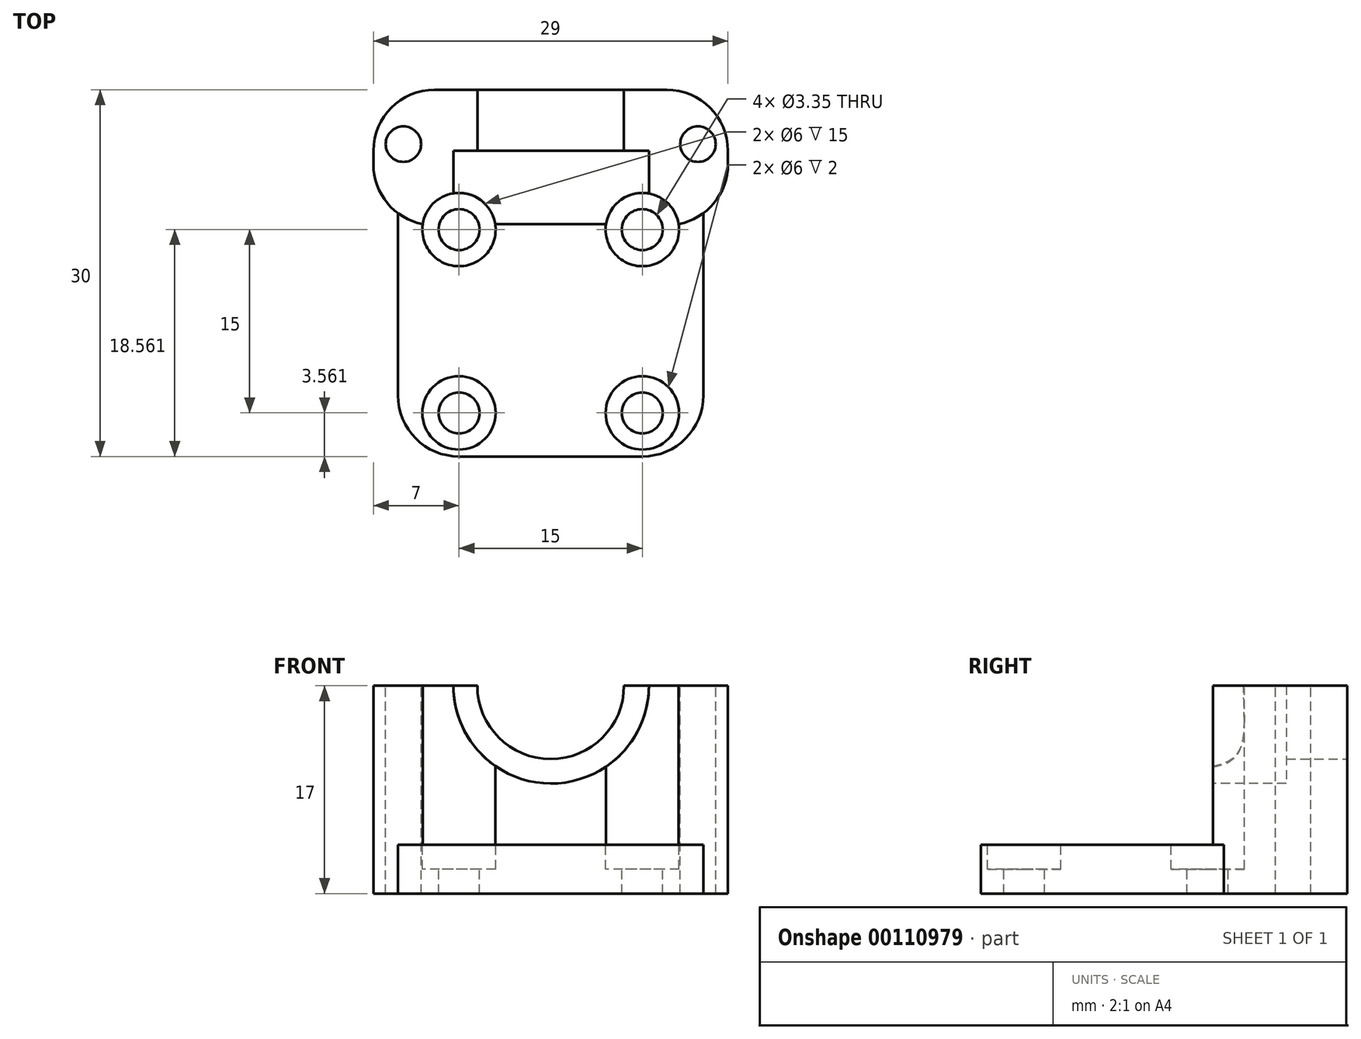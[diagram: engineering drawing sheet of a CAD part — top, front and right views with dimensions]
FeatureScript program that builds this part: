
annotation { "Feature Type Name" : "Feature", "Feature Type Description" : "" }
export const myFeature = defineFeature(function(context is Context, id is Id, definition is map)
    precondition{}
    {
        {
            var Q0;
            Q0=qCreatedBy(makeId("Top.planeOp"),FACE);
            var sketch = newSketch(context, id + "F0", { "sketchPlane" : qUnion([Q0])});
            skLineSegment(sketch, "E0.bottom", {"start": v(0, 0) * mm, "end": v(25, 0) * mm});
            skLineSegment(sketch, "E0.top", {"start": v(0, 30) * mm, "end": v(25, 30) * mm});
            skLineSegment(sketch, "E0.left", {"start": v(0, 0) * mm, "end": v(0, 30) * mm});
            skLineSegment(sketch, "E0.right", {"start": v(25, 0) * mm, "end": v(25, 30) * mm});
            skSolve(sketch);
        }
        {
            var Q0;
            Q0=qSketchRegion(id+"F0",true);
            extrude(context, id + "F1", {"entities" : qUnion([Q0]), "depth" : 4 * mm});
        }
        {
            var Q0;
            Q0=makeQuery(id+"F1.opExtrude","CAP_FACE",FACE,{"disambiguationData":[OSD([sQuery(id+"F0.wireOp",EDGE,"E0.bottom"),sQuery(id+"F0.wireOp",EDGE,"E0.top"),sQuery(id+"F0.wireOp",EDGE,"E0.left"),sQuery(id+"F0.wireOp",EDGE,"E0.right")])],"isStart":false});
            var sketch = newSketch(context, id + "F2", { "sketchPlane" : qUnion([Q0])});
            skLineSegment(sketch, "E1.bottom", {"start": v(0, 30) * mm, "end": v(25, 30) * mm});
            skLineSegment(sketch, "E1.top", {"start": v(0, 19) * mm, "end": v(25, 19) * mm});
            skLineSegment(sketch, "E1.left", {"start": v(0, 30) * mm, "end": v(0, 19) * mm});
            skLineSegment(sketch, "E1.right", {"start": v(25, 30) * mm, "end": v(25, 19) * mm});
            skSolve(sketch);
        }
        {
            var Q0;
            Q0=qSketchRegion(id+"F2",true);
            extrude(context, id + "F3", {"entities" : qUnion([Q0]), "operationType" : NewBodyOperationType.ADD, "depth" : 13 * mm});
        }
        {
            var Q0;
            Q0=makeQuery(id+"F1.opExtrude","CAP_FACE",FACE,{"disambiguationData":[OSD([sQuery(id+"F0.wireOp",EDGE,"E0.bottom"),sQuery(id+"F0.wireOp",EDGE,"E0.top"),sQuery(id+"F0.wireOp",EDGE,"E0.left"),sQuery(id+"F0.wireOp",EDGE,"E0.right")])],"isStart":false});
            var sketch = newSketch(context, id + "F4", { "sketchPlane" : qUnion([Q0])});
            skCircle(sketch, "E2", {"center": v(5, 18.56) * mm, "radius": 1.68 * mm});
            skCircle(sketch, "E3", {"center": v(20, 18.56) * mm, "radius": 1.68 * mm});
            skCircle(sketch, "E4", {"center": v(5, 3.56) * mm, "radius": 1.68 * mm});
            skCircle(sketch, "E5", {"center": v(20, 3.56) * mm, "radius": 1.68 * mm});
            skLineSegment(sketch, "E6", {"start": v(5, 18.56) * mm, "end": v(0, 18.56) * mm});
            skLineSegment(sketch, "E7", {"start": v(20, 3.56) * mm, "end": v(25, 3.56) * mm});
            skCircle(sketch, "E8", {"center": v(5, 18.56) * mm, "radius": 3 * mm});
            skCircle(sketch, "E9", {"center": v(20, 18.56) * mm, "radius": 3 * mm});
            skCircle(sketch, "E10", {"center": v(5, 3.56) * mm, "radius": 3 * mm});
            skCircle(sketch, "E11", {"center": v(20, 3.56) * mm, "radius": 3 * mm});
            skSolve(sketch);
        }
        {
            var Q0;
            Q0=makeQuery(id+"F4.imprint","IMPRINT",FACE,{"disambiguationData":[TD([[makeQuery(id+"F4.imprint","IMPRINT",EDGE,{"derivedFrom":sQuery(id+"F4.wireOp",EDGE,"E2")}),1.0]])]});
            var Q1;
            Q1=makeQuery(id+"F4.imprint","IMPRINT",FACE,{"disambiguationData":[TD([[makeQuery(id+"F4.imprint","IMPRINT",EDGE,{"derivedFrom":sQuery(id+"F4.wireOp",EDGE,"E3")}),1.0]])]});
            var Q2;
            Q2=makeQuery(id+"F4.imprint","IMPRINT",FACE,{"disambiguationData":[TD([[makeQuery(id+"F4.imprint","IMPRINT",EDGE,{"derivedFrom":sQuery(id+"F4.wireOp",EDGE,"E5")}),1.0]])]});
            var Q3;
            Q3=makeQuery(id+"F4.imprint","IMPRINT",FACE,{"disambiguationData":[TD([[makeQuery(id+"F4.imprint","IMPRINT",EDGE,{"derivedFrom":sQuery(id+"F4.wireOp",EDGE,"E4")}),1.0]])]});
            var Q4;
            {var subQ0=sQuery(id+"F4.wireOp",EDGE,"E2");var subQ1=makeQuery(id+"F3.opExtrude","CAP_EDGE",EDGE,{"disambiguationData":[OSD([sQuery(id+"F2.wireOp",EDGE,"E1.top")])],"isStart":true});var subQ2=makeQuery(id+"F4.imprint","INTERSECT",VERTEX,{"disambiguationData":[OD(0.0)],"derivedFrom":[subQ1,subQ0]});Q4=makeQuery(id+"F4.imprint","IMPRINT",FACE,{"disambiguationData":[TD([[makeQuery(id+"F4.imprint","IMPRINT",EDGE,{"disambiguationData":[TD([[subQ2,1.0]])],"derivedFrom":subQ0}),1.0]])]});}
            extrude(context, id + "F5", {"entities" : qUnion([Q0, Q1, Q2, Q3, Q4]), "operationType" : NewBodyOperationType.REMOVE, "oppositeDirection" : true, "depth" : 25 * mm, "hasSecondDirection" : true, "secondDirectionOppositeDirection" : false, "secondDirectionDepth" : 25 * mm});
        }
        {
            var Q0;
            Q0=makeQuery(id+"F3.boolean.opBoolean","MERGE",FACE,{"derivedFrom":[makeQuery(id+"F1.opExtrude","SWEPT_FACE",FACE,{"disambiguationData":[OSD([sQuery(id+"F0.wireOp",EDGE,"E0.top")])]}),makeQuery(id+"F3.opExtrude","SWEPT_FACE",FACE,{"disambiguationData":[OSD([sQuery(id+"F2.wireOp",EDGE,"E1.bottom")])]})]});
            var sketch = newSketch(context, id + "F6", { "sketchPlane" : qUnion([Q0])});
            skCircle(sketch, "E12", {"center": v(-12.5, 17) * mm, "radius": 6 * mm});
            skSolve(sketch);
        }
        {
            var Q0;
            {var subQ0=makeQuery(id+"F3.opExtrude","CAP_EDGE",EDGE,{"disambiguationData":[OSD([sQuery(id+"F2.wireOp",EDGE,"E1.bottom")])],"isStart":false});var subQ1=sQuery(id+"F6.wireOp",EDGE,"E12");var subQ3=makeQuery(id+"F6.imprint","INTERSECT",VERTEX,{"disambiguationData":[OD(0.0)],"derivedFrom":[subQ0,subQ1]});Q0=makeQuery(id+"F6.imprint","IMPRINT",FACE,{"disambiguationData":[TD([[makeQuery(id+"F6.imprint","IMPRINT",EDGE,{"disambiguationData":[TD([[subQ3,1.0]])],"derivedFrom":subQ1}),1.0]])]});}
            extrude(context, id + "F7", {"entities" : qUnion([Q0]), "operationType" : NewBodyOperationType.REMOVE, "oppositeDirection" : true, "depth" : 6 * mm});
        }
        {
            var Q0;
            Q0=makeQuery(id+"F3.opExtrude","SWEPT_FACE",FACE,{"disambiguationData":[OSD([sQuery(id+"F2.wireOp",EDGE,"E1.top")])]});
            var sketch = newSketch(context, id + "F8", { "sketchPlane" : qUnion([Q0])});
            skCircle(sketch, "E13", {"center": v(12.54, 17) * mm, "radius": 8 * mm});
            skSolve(sketch);
        }
        {
            var Q0;
            Q0=qSketchRegion(id+"F8",true);
            extrude(context, id + "F9", {"entities" : qUnion([Q0]), "operationType" : NewBodyOperationType.REMOVE, "oppositeDirection" : true, "depth" : 6 * mm});
        }
        {
            var Q0;
            Q0=makeQuery(id+"F4.imprint","IMPRINT",FACE,{"disambiguationData":[TD([[makeQuery(id+"F4.imprint","IMPRINT",EDGE,{"derivedFrom":sQuery(id+"F4.wireOp",EDGE,"E2")}),-1.0]])]});
            var Q1;
            Q1=makeQuery(id+"F4.imprint","IMPRINT",FACE,{"disambiguationData":[TD([[makeQuery(id+"F4.imprint","IMPRINT",EDGE,{"derivedFrom":sQuery(id+"F4.wireOp",EDGE,"E3")}),-1.0]])]});
            var Q2;
            Q2=makeQuery(id+"F4.imprint","IMPRINT",FACE,{"disambiguationData":[TD([[makeQuery(id+"F4.imprint","IMPRINT",EDGE,{"derivedFrom":sQuery(id+"F4.wireOp",EDGE,"E5")}),-1.0]])]});
            var Q3;
            Q3=makeQuery(id+"F4.imprint","IMPRINT",FACE,{"disambiguationData":[TD([[makeQuery(id+"F4.imprint","IMPRINT",EDGE,{"derivedFrom":sQuery(id+"F4.wireOp",EDGE,"E4")}),-1.0]])]});
            extrude(context, id + "F10", {"entities" : qUnion([Q0, Q1, Q2, Q3]), "operationType" : NewBodyOperationType.REMOVE, "oppositeDirection" : true, "depth" : 2 * mm, "hasSecondDirection" : true, "secondDirectionOppositeDirection" : false, "secondDirectionDepth" : 25 * mm});
        }
        {
            var Q0;
            Q0=makeQuery(id+"F1.opExtrude","SWEPT_EDGE",EDGE,{"disambiguationData":[OSD([sQuery(id+"F0.wireOp",EDGE,"E0.bottom"),sQuery(id+"F0.wireOp",EDGE,"E0.left")])]});
            var Q1;
            Q1=makeQuery(id+"F1.opExtrude","SWEPT_EDGE",EDGE,{"disambiguationData":[OSD([sQuery(id+"F0.wireOp",EDGE,"E0.bottom"),sQuery(id+"F0.wireOp",EDGE,"E0.right")])]});
            fillet(context, id + "F11", {"entities" : qUnion([Q0, Q1]), "radius" : 5 * mm, "tangentPropagation" : true, "allowEdgeOverflow" : false});
        }
        {
            var Q0;
            Q0=makeQuery(id+"F3.boolean.opBoolean","MERGE",FACE,{"derivedFrom":[makeQuery(id+"F1.opExtrude","SWEPT_FACE",FACE,{"disambiguationData":[OSD([sQuery(id+"F0.wireOp",EDGE,"E0.left")])]}),makeQuery(id+"F3.opExtrude","SWEPT_FACE",FACE,{"disambiguationData":[OSD([sQuery(id+"F2.wireOp",EDGE,"E1.left")])]})]});
            var sketch = newSketch(context, id + "F12", { "sketchPlane" : qUnion([Q0])});
            skLineSegment(sketch, "E14.bottom", {"start": v(-30, 0) * mm, "end": v(-19, 0) * mm});
            skLineSegment(sketch, "E14.top", {"start": v(-30, 17) * mm, "end": v(-19, 17) * mm});
            skLineSegment(sketch, "E14.left", {"start": v(-30, 0) * mm, "end": v(-30, 17) * mm});
            skLineSegment(sketch, "E14.right", {"start": v(-19, 0) * mm, "end": v(-19, 17) * mm});
            skSolve(sketch);
        }
        {
            var Q0;
            {var subQ3=sQuery(id+"F12.wireOp",EDGE,"E14.bottom");Q0=makeQuery(id+"F12.imprint","IMPRINT",FACE,{"disambiguationData":[TD([[makeQuery(id+"F12.imprint","IMPRINT",EDGE,{"derivedFrom":subQ3}),-1.0]])]});}
            extrude(context, id + "F13", {"entities" : qUnion([Q0]), "operationType" : NewBodyOperationType.ADD, "depth" : 2 * mm});
        }
        {
            var Q0;
            Q0=makeQuery(id+"F3.boolean.opBoolean","MERGE",FACE,{"derivedFrom":[makeQuery(id+"F1.opExtrude","SWEPT_FACE",FACE,{"disambiguationData":[OSD([sQuery(id+"F0.wireOp",EDGE,"E0.right")])]}),makeQuery(id+"F3.opExtrude","SWEPT_FACE",FACE,{"disambiguationData":[OSD([sQuery(id+"F2.wireOp",EDGE,"E1.right")])]})]});
            var sketch = newSketch(context, id + "F14", { "sketchPlane" : qUnion([Q0])});
            skLineSegment(sketch, "E15.bottom", {"start": v(30, 0) * mm, "end": v(19, 0) * mm});
            skLineSegment(sketch, "E15.top", {"start": v(30, 17) * mm, "end": v(19, 17) * mm});
            skLineSegment(sketch, "E15.left", {"start": v(30, 0) * mm, "end": v(30, 17) * mm});
            skLineSegment(sketch, "E15.right", {"start": v(19, 0) * mm, "end": v(19, 17) * mm});
            skSolve(sketch);
        }
        {
            var Q0;
            Q0=qSketchRegion(id+"F14",true);
            extrude(context, id + "F15", {"entities" : qUnion([Q0]), "operationType" : NewBodyOperationType.ADD, "depth" : 2 * mm});
        }
        {
            var Q0;
            {var subQ0=sQuery(id+"F2.wireOp",EDGE,"E1.bottom");var subQ1=sQuery(id+"F2.wireOp",EDGE,"E1.top");var subQ2=sQuery(id+"F2.wireOp",EDGE,"E1.left");Q0=makeQuery(id+"F9.boolean.opBoolean","SPLIT",FACE,{"disambiguationData":[TD([makeQuery(id+"F1.opExtrude","SWEPT_FACE",FACE,{"disambiguationData":[OSD([sQuery(id+"F0.wireOp",EDGE,"E0.left")])]})])],"derivedFrom":makeQuery(id+"F3.opExtrude","CAP_FACE",FACE,{"disambiguationData":[OSD([subQ0,subQ1,subQ2,sQuery(id+"F2.wireOp",EDGE,"E1.right")])],"isStart":false})});}
            var sketch = newSketch(context, id + "F16", { "sketchPlane" : qUnion([Q0])});
            skCircle(sketch, "E16", {"center": v(0.45, 25.55) * mm, "radius": 1.45 * mm});
            skCircle(sketch, "E17", {"center": v(24.55, 25.55) * mm, "radius": 1.45 * mm});
            skSolve(sketch);
        }
        {
            var Q0;
            Q0=qSketchRegion(id+"F16",true);
            extrude(context, id + "F17", {"entities" : qUnion([Q0]), "operationType" : NewBodyOperationType.REMOVE, "oppositeDirection" : true, "depth" : 25 * mm});
        }
        {
            var Q0;
            Q0=makeQuery(id+"F13.opExtrude","CAP_EDGE",EDGE,{"disambiguationData":[OSD([sQuery(id+"F12.wireOp",EDGE,"E14.right")])],"isStart":false});
            var Q1;
            Q1=makeQuery(id+"F13.opExtrude","CAP_EDGE",EDGE,{"disambiguationData":[OSD([sQuery(id+"F12.wireOp",EDGE,"E14.left")])],"isStart":false});
            var Q2;
            Q2=makeQuery(id+"F15.opExtrude","CAP_EDGE",EDGE,{"disambiguationData":[OSD([sQuery(id+"F14.wireOp",EDGE,"E15.left")])],"isStart":false});
            var Q3;
            Q3=makeQuery(id+"F15.opExtrude","CAP_EDGE",EDGE,{"disambiguationData":[OSD([sQuery(id+"F14.wireOp",EDGE,"E15.right")])],"isStart":false});
            fillet(context, id + "F18", {"entities" : qUnion([Q0, Q1, Q2, Q3]), "radius" : 5 * mm, "tangentPropagation" : true, "allowEdgeOverflow" : false});
        }
    });
